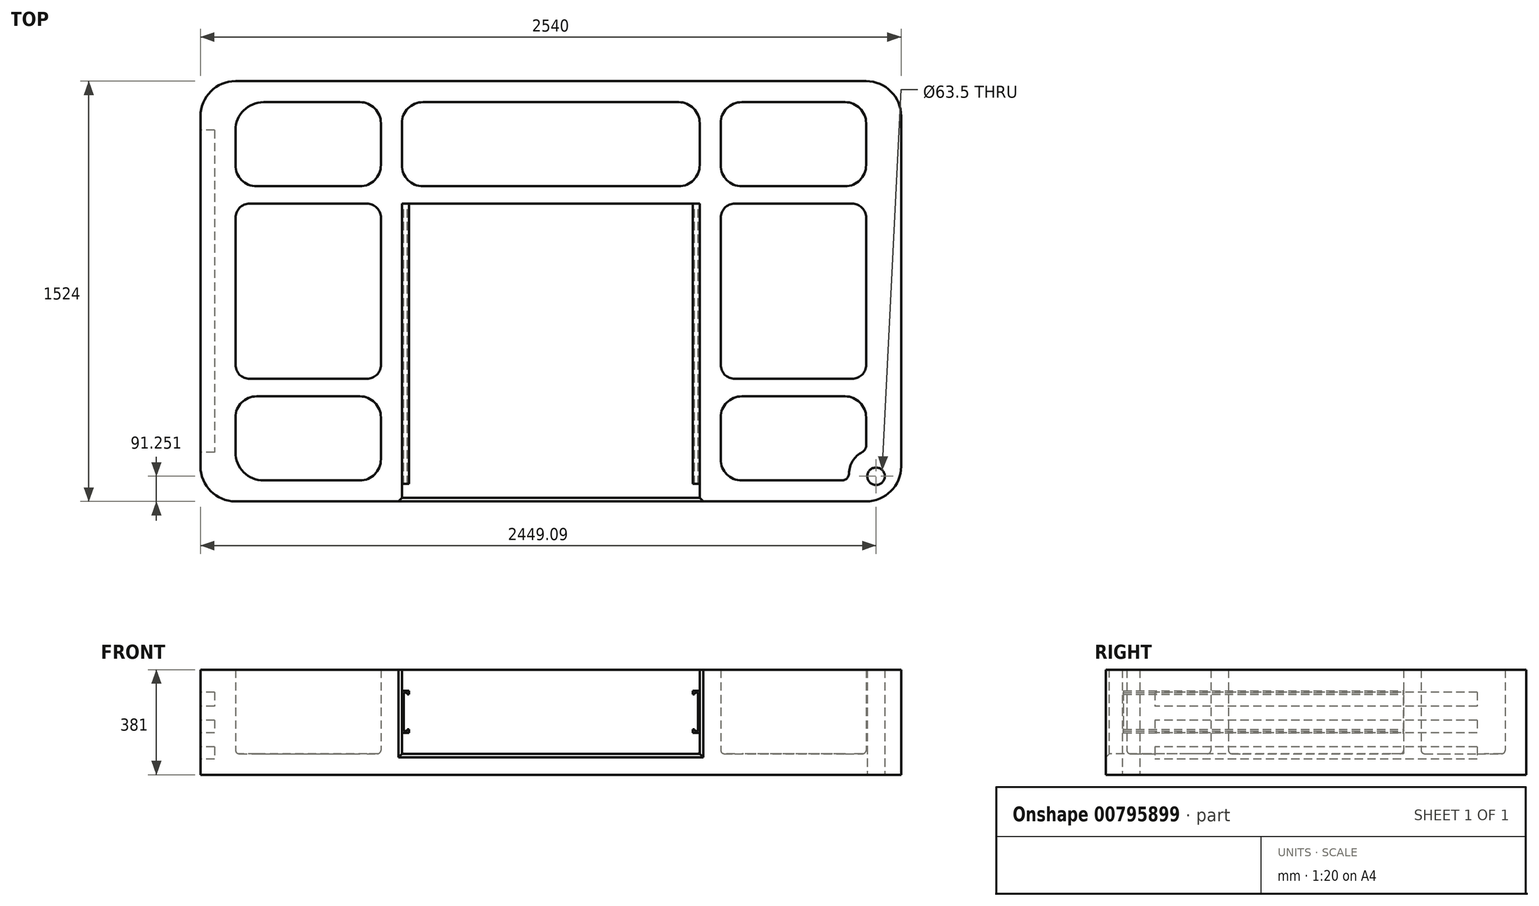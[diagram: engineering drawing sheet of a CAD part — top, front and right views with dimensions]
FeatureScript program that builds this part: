
annotation { "Feature Type Name" : "Feature", "Feature Type Description" : "" }
export const myFeature = defineFeature(function(context is Context, id is Id, definition is map)
    precondition{}
    {
        {
            var Q0;
            Q0=qCreatedBy(makeId("Top.planeOp"),FACE);
            var sketch = newSketch(context, id + "F0", { "sketchPlane" : qUnion([Q0])});
            skLineSegment(sketch, "E0.bottom", {"start": v(-254, 266.7) * mm, "end": v(500.38, 266.7) * mm});
            skLineSegment(sketch, "E0.top", {"start": v(-254, -266.7) * mm, "end": v(500.38, -266.7) * mm});
            skLineSegment(sketch, "E0.left", {"start": v(-254, 266.7) * mm, "end": v(-254, -266.7) * mm});
            skLineSegment(sketch, "E0.right", {"start": v(500.38, 266.7) * mm, "end": v(500.38, -266.7) * mm});
            skSolve(sketch);
        }
        {
            var Q0;
            Q0=qCreatedBy(makeId("Top.planeOp"),FACE);
            var sketch = newSketch(context, id + "F1", { "sketchPlane" : qUnion([Q0])});
            skLineSegment(sketch, "E1.bottom", {"start": v(1270, -762) * mm, "end": v(-1270, -762) * mm});
            skLineSegment(sketch, "E1.top", {"start": v(1270, 762) * mm, "end": v(-1270, 762) * mm});
            skLineSegment(sketch, "E1.left", {"start": v(1270, -762) * mm, "end": v(1270, 762) * mm});
            skLineSegment(sketch, "E1.right", {"start": v(-1270, -762) * mm, "end": v(-1270, 762) * mm});
            skPoint(sketch, "E1.middle", {"position": v(0, 0) * mm});
            skLineSegment(sketch, "E2.bottom", {"start": v(-692.15, 685.8) * mm, "end": v(-1041.4, 685.8) * mm});
            skLineSegment(sketch, "E2.top", {"start": v(-692.15, 381) * mm, "end": v(-1066.8, 381) * mm});
            skLineSegment(sketch, "E2.left", {"start": v(-615.95, 609.6) * mm, "end": v(-615.95, 457.2) * mm});
            skLineSegment(sketch, "E2.right", {"start": v(-1143, 584.2) * mm, "end": v(-1143, 457.2) * mm});
            skPoint(sketch, "E2.middle", {"position": v(-879.48, 533.4) * mm});
            skLineSegment(sketch, "E3.left", {"start": v(-539.75, 609.6) * mm, "end": v(-539.75, 457.2) * mm});
            skPoint(sketch, "E3.middle", {"position": v(0, 528.9) * mm});
            skLineSegment(sketch, "E4", {"start": v(0, 837.18) * mm, "end": v(0, -847.88) * mm, "construction": true});
            skPoint(sketch, "E4.startSnap0", {"position": v(0, 762) * mm});
            skLineSegment(sketch, "E5", {"start": v(-857.73, 0) * mm, "end": v(882.55, 0) * mm, "construction": true});
            skPoint(sketch, "E5.startSnap0", {"position": v(-1270, 0) * mm});
            skLineSegment(sketch, "E6", {"start": v(-463.55, 685.8) * mm, "end": v(0, 685.8) * mm});
            skLineSegment(sketch, "E7", {"start": v(0, 685.8) * mm, "end": v(0, 381) * mm});
            skLineSegment(sketch, "E8", {"start": v(0, 381) * mm, "end": v(-463.55, 381) * mm});
            skLineSegment(sketch, "E9.bottom", {"start": v(-539.75, 317.5) * mm, "end": v(539.75, 317.5) * mm});
            skLineSegment(sketch, "E9.top", {"start": v(-539.75, -317.5) * mm, "end": v(539.75, -317.5) * mm});
            skLineSegment(sketch, "E9.left", {"start": v(-539.75, 317.5) * mm, "end": v(-539.75, -317.5) * mm});
            skLineSegment(sketch, "E9.right", {"start": v(539.75, 317.5) * mm, "end": v(539.75, -317.5) * mm});
            skLineSegment(sketch, "E10.bottom", {"start": v(-1092.2, 317.5) * mm, "end": v(-666.75, 317.5) * mm});
            skLineSegment(sketch, "E10.top", {"start": v(-1092.2, -317.5) * mm, "end": v(-666.75, -317.5) * mm});
            skLineSegment(sketch, "E10.left", {"start": v(-1143, 266.7) * mm, "end": v(-1143, -266.7) * mm});
            skLineSegment(sketch, "E10.right", {"start": v(-615.95, 266.7) * mm, "end": v(-615.95, -266.7) * mm});
            skPoint(sketch, "E10.middle", {"position": v(-879.48, 0) * mm});
            skLineSegment(sketch, "E11.MirrorCS", {"start": v(0, 381) * mm, "end": v(463.55, 381) * mm});
            skLineSegment(sketch, "E12.MirrorCS", {"start": v(539.75, 609.6) * mm, "end": v(539.75, 457.2) * mm});
            skLineSegment(sketch, "E13.MirrorCS", {"start": v(463.55, 685.8) * mm, "end": v(0, 685.8) * mm});
            skLineSegment(sketch, "E14.MirrorCS", {"start": v(692.15, 685.8) * mm, "end": v(1066.8, 685.8) * mm});
            skLineSegment(sketch, "E15.MirrorCS", {"start": v(615.95, 609.6) * mm, "end": v(615.95, 457.2) * mm});
            skLineSegment(sketch, "E16.MirrorCS", {"start": v(692.15, 381) * mm, "end": v(1066.8, 381) * mm});
            skLineSegment(sketch, "E17.MirrorCS", {"start": v(1143, 609.6) * mm, "end": v(1143, 457.2) * mm});
            skLineSegment(sketch, "E18.MirrorCS", {"start": v(615.95, 266.7) * mm, "end": v(615.95, -266.7) * mm});
            skLineSegment(sketch, "E19.MirrorCS", {"start": v(1092.2, -317.5) * mm, "end": v(666.75, -317.5) * mm});
            skLineSegment(sketch, "E20.MirrorCS", {"start": v(1143, 266.7) * mm, "end": v(1143, -266.7) * mm});
            skLineSegment(sketch, "E21.MirrorCS", {"start": v(1092.2, 317.5) * mm, "end": v(666.75, 317.5) * mm});
            skLineSegment(sketch, "E22.MirrorCS", {"start": v(-1143, -584.2) * mm, "end": v(-1143, -457.2) * mm});
            skLineSegment(sketch, "E23.MirrorCS", {"start": v(-692.15, -685.8) * mm, "end": v(-1041.4, -685.8) * mm});
            skLineSegment(sketch, "E24.MirrorCS", {"start": v(-615.95, -609.6) * mm, "end": v(-615.95, -457.2) * mm});
            skLineSegment(sketch, "E25.MirrorCS", {"start": v(-692.15, -381) * mm, "end": v(-1066.8, -381) * mm});
            skLineSegment(sketch, "E26.MirrorCS", {"start": v(0, -381) * mm, "end": v(-463.55, -381) * mm});
            skLineSegment(sketch, "E27.MirrorCS", {"start": v(-539.75, -609.6) * mm, "end": v(-539.75, -457.2) * mm});
            skLineSegment(sketch, "E28.MirrorCS", {"start": v(-463.55, -685.8) * mm, "end": v(0, -685.8) * mm});
            skLineSegment(sketch, "E29.MirrorCS", {"start": v(463.55, -685.8) * mm, "end": v(0, -685.8) * mm});
            skLineSegment(sketch, "E30.MirrorCS", {"start": v(0, -381) * mm, "end": v(463.55, -381) * mm});
            skLineSegment(sketch, "E31.MirrorCS", {"start": v(539.75, -609.6) * mm, "end": v(539.75, -457.2) * mm});
            skLineSegment(sketch, "E32.MirrorCS", {"start": v(692.15, -381) * mm, "end": v(1066.8, -381) * mm});
            skLineSegment(sketch, "E33.MirrorCS", {"start": v(615.95, -609.6) * mm, "end": v(615.95, -457.2) * mm});
            skLineSegment(sketch, "E34.MirrorCS", {"start": v(692.15, -685.8) * mm, "end": v(1066.8, -685.8) * mm});
            skLineSegment(sketch, "E35.MirrorCS", {"start": v(1143, -609.6) * mm, "end": v(1143, -457.2) * mm});
            skPoint(sketch, "E36.visualSharp", {"position": v(615.95, 685.8) * mm});
            skArc(sketch, "E36.filletArc", {"start": v(692.15, 685.8) * mm, "mid": v(638.27, 663.48) * mm, "end": v(615.95, 609.6) * mm});
            skPoint(sketch, "E37.visualSharp", {"position": v(615.95, 381) * mm});
            skArc(sketch, "E37.filletArc", {"start": v(615.95, 457.2) * mm, "mid": v(638.27, 403.32) * mm, "end": v(692.15, 381) * mm});
            skPoint(sketch, "E38.visualSharp", {"position": v(1143, 381) * mm});
            skArc(sketch, "E38.filletArc", {"start": v(1066.8, 381) * mm, "mid": v(1120.68, 403.32) * mm, "end": v(1143, 457.2) * mm});
            skPoint(sketch, "E39.visualSharp", {"position": v(1143, -381) * mm});
            skArc(sketch, "E39.filletArc", {"start": v(1143, -457.2) * mm, "mid": v(1120.68, -403.32) * mm, "end": v(1066.8, -381) * mm});
            skPoint(sketch, "E40.visualSharp", {"position": v(1143, -685.8) * mm});
            skPoint(sketch, "E41.visualSharp", {"position": v(615.95, -381) * mm});
            skArc(sketch, "E41.filletArc", {"start": v(692.15, -381) * mm, "mid": v(638.27, -403.32) * mm, "end": v(615.95, -457.2) * mm});
            skPoint(sketch, "E42.visualSharp", {"position": v(615.95, -685.8) * mm});
            skArc(sketch, "E42.filletArc", {"start": v(615.95, -609.6) * mm, "mid": v(638.27, -663.48) * mm, "end": v(692.15, -685.8) * mm});
            skPoint(sketch, "E43.visualSharp", {"position": v(-615.95, -381) * mm});
            skArc(sketch, "E43.filletArc", {"start": v(-615.95, -457.2) * mm, "mid": v(-638.27, -403.32) * mm, "end": v(-692.15, -381) * mm});
            skPoint(sketch, "E44.visualSharp", {"position": v(-615.95, -685.8) * mm});
            skArc(sketch, "E44.filletArc", {"start": v(-692.15, -685.8) * mm, "mid": v(-638.27, -663.48) * mm, "end": v(-615.95, -609.6) * mm});
            skPoint(sketch, "E45.visualSharp", {"position": v(-1143, -381) * mm});
            skArc(sketch, "E45.filletArc", {"start": v(-1066.8, -381) * mm, "mid": v(-1120.68, -403.32) * mm, "end": v(-1143, -457.2) * mm});
            skPoint(sketch, "E46.visualSharp", {"position": v(-539.75, -381) * mm});
            skArc(sketch, "E46.filletArc", {"start": v(-463.55, -381) * mm, "mid": v(-517.43, -403.32) * mm, "end": v(-539.75, -457.2) * mm});
            skPoint(sketch, "E47.visualSharp", {"position": v(-539.75, -685.8) * mm});
            skArc(sketch, "E47.filletArc", {"start": v(-539.75, -609.6) * mm, "mid": v(-517.43, -663.48) * mm, "end": v(-463.55, -685.8) * mm});
            skPoint(sketch, "E48.visualSharp", {"position": v(539.75, -381) * mm});
            skArc(sketch, "E48.filletArc", {"start": v(539.75, -457.2) * mm, "mid": v(517.43, -403.32) * mm, "end": v(463.55, -381) * mm});
            skPoint(sketch, "E49.visualSharp", {"position": v(539.75, -685.8) * mm});
            skArc(sketch, "E49.filletArc", {"start": v(463.55, -685.8) * mm, "mid": v(517.43, -663.48) * mm, "end": v(539.75, -609.6) * mm});
            skPoint(sketch, "E50.visualSharp", {"position": v(-539.75, 685.8) * mm});
            skArc(sketch, "E50.filletArc", {"start": v(-463.55, 685.8) * mm, "mid": v(-517.43, 663.48) * mm, "end": v(-539.75, 609.6) * mm});
            skPoint(sketch, "E51.visualSharp", {"position": v(-539.75, 381) * mm});
            skArc(sketch, "E51.filletArc", {"start": v(-539.75, 457.2) * mm, "mid": v(-517.43, 403.32) * mm, "end": v(-463.55, 381) * mm});
            skPoint(sketch, "E52.visualSharp", {"position": v(539.75, 685.8) * mm});
            skArc(sketch, "E52.filletArc", {"start": v(539.75, 609.6) * mm, "mid": v(517.43, 663.48) * mm, "end": v(463.55, 685.8) * mm});
            skPoint(sketch, "E53.visualSharp", {"position": v(539.75, 381) * mm});
            skArc(sketch, "E53.filletArc", {"start": v(463.55, 381) * mm, "mid": v(517.43, 403.32) * mm, "end": v(539.75, 457.2) * mm});
            skPoint(sketch, "E54.visualSharp", {"position": v(-615.95, 685.8) * mm});
            skArc(sketch, "E54.filletArc", {"start": v(-615.95, 609.6) * mm, "mid": v(-638.27, 663.48) * mm, "end": v(-692.15, 685.8) * mm});
            skPoint(sketch, "E55.visualSharp", {"position": v(-1143, 685.8) * mm});
            skPoint(sketch, "E56.visualSharp", {"position": v(-1143, 381) * mm});
            skArc(sketch, "E56.filletArc", {"start": v(-1143, 457.2) * mm, "mid": v(-1120.68, 403.32) * mm, "end": v(-1066.8, 381) * mm});
            skPoint(sketch, "E57.visualSharp", {"position": v(-615.95, 381) * mm});
            skArc(sketch, "E57.filletArc", {"start": v(-692.15, 381) * mm, "mid": v(-638.27, 403.32) * mm, "end": v(-615.95, 457.2) * mm});
            skPoint(sketch, "E58.visualSharp", {"position": v(-615.95, 317.5) * mm});
            skArc(sketch, "E58.filletArc", {"start": v(-615.95, 266.7) * mm, "mid": v(-630.83, 302.62) * mm, "end": v(-666.75, 317.5) * mm});
            skPoint(sketch, "E59.visualSharp", {"position": v(-1143, 317.5) * mm});
            skArc(sketch, "E59.filletArc", {"start": v(-1092.2, 317.5) * mm, "mid": v(-1128.12, 302.62) * mm, "end": v(-1143, 266.7) * mm});
            skPoint(sketch, "E60.visualSharp", {"position": v(-1143, -317.5) * mm});
            skArc(sketch, "E60.filletArc", {"start": v(-1143, -266.7) * mm, "mid": v(-1128.12, -302.62) * mm, "end": v(-1092.2, -317.5) * mm});
            skPoint(sketch, "E61.visualSharp", {"position": v(-615.95, -317.5) * mm});
            skArc(sketch, "E61.filletArc", {"start": v(-666.75, -317.5) * mm, "mid": v(-630.83, -302.62) * mm, "end": v(-615.95, -266.7) * mm});
            skPoint(sketch, "E62.visualSharp", {"position": v(615.95, 317.5) * mm});
            skArc(sketch, "E62.filletArc", {"start": v(666.75, 317.5) * mm, "mid": v(630.83, 302.62) * mm, "end": v(615.95, 266.7) * mm});
            skPoint(sketch, "E63.visualSharp", {"position": v(1143, 317.5) * mm});
            skArc(sketch, "E63.filletArc", {"start": v(1143, 266.7) * mm, "mid": v(1128.12, 302.62) * mm, "end": v(1092.2, 317.5) * mm});
            skPoint(sketch, "E64.visualSharp", {"position": v(1143, -317.5) * mm});
            skArc(sketch, "E64.filletArc", {"start": v(1092.2, -317.5) * mm, "mid": v(1128.12, -302.62) * mm, "end": v(1143, -266.7) * mm});
            skPoint(sketch, "E65.visualSharp", {"position": v(615.95, -317.5) * mm});
            skArc(sketch, "E65.filletArc", {"start": v(615.95, -266.7) * mm, "mid": v(630.83, -302.62) * mm, "end": v(666.75, -317.5) * mm});
            skLineSegment(sketch, "E66.MirrorCS", {"start": v(857.73, 0) * mm, "end": v(-882.55, 0) * mm, "construction": true});
            skArc(sketch, "E67.filletArc", {"start": v(-1143, -584.2) * mm, "mid": v(-1113.24, -656.04) * mm, "end": v(-1041.4, -685.8) * mm});
            skArc(sketch, "E68.filletArc", {"start": v(-1041.4, 685.8) * mm, "mid": v(-1113.24, 656.04) * mm, "end": v(-1143, 584.2) * mm});
            skArc(sketch, "E69.filletArc", {"start": v(1143, 609.6) * mm, "mid": v(1120.68, 663.48) * mm, "end": v(1066.8, 685.8) * mm});
            skArc(sketch, "E70.filletArc", {"start": v(1066.8, -685.8) * mm, "mid": v(1120.68, -663.48) * mm, "end": v(1143, -609.6) * mm});
            skSolve(sketch);
        }
        {
            var Q0;
            Q0=qSketchRegion(id+"F1",true);
            extrude(context, id + "F2", {"entities" : qUnion([Q0]), "depth" : 381 * mm, "offsetDistance" : 25.4 * mm});
        }
        {
            var Q0;
            Q0=makeQuery(id+"F2.opExtrude","SWEPT_EDGE",EDGE,{"disambiguationData":[OSD([sQuery(id+"F1.wireOp",EDGE,"E1.bottom"),sQuery(id+"F1.wireOp",EDGE,"E1.right")])]});
            var Q1;
            Q1=makeQuery(id+"F2.opExtrude","SWEPT_EDGE",EDGE,{"disambiguationData":[OSD([sQuery(id+"F1.wireOp",EDGE,"E1.bottom"),sQuery(id+"F1.wireOp",EDGE,"E1.left")])]});
            var Q2;
            Q2=makeQuery(id+"F2.opExtrude","SWEPT_EDGE",EDGE,{"disambiguationData":[OSD([sQuery(id+"F1.wireOp",EDGE,"E1.top"),sQuery(id+"F1.wireOp",EDGE,"E1.right")])]});
            var Q3;
            Q3=makeQuery(id+"F2.opExtrude","SWEPT_EDGE",EDGE,{"disambiguationData":[OSD([sQuery(id+"F1.wireOp",EDGE,"E1.top"),sQuery(id+"F1.wireOp",EDGE,"E1.left")])]});
            fillet(context, id + "F3", {"entities" : qUnion([Q0, Q1, Q2, Q3]), "radius" : 127 * mm, "tangentPropagation" : true, "allowEdgeOverflow" : false});
        }
        {
            var Q0;
            Q0=makeQuery(id+"F2.opExtrude","CAP_FACE",FACE,{"disambiguationData":[OSD([sQuery(id+"F1.wireOp",EDGE,"E1.bottom"),sQuery(id+"F1.wireOp",EDGE,"E1.top"),sQuery(id+"F1.wireOp",EDGE,"E1.left"),sQuery(id+"F1.wireOp",EDGE,"E1.right")])],"isStart":false});
            var sketch = newSketch(context, id + "F4", { "sketchPlane" : qUnion([Q0])});
            skSolve(sketch);
        }
        {
            var Q0;
            Q0=makeQuery(id+"F2.opExtrude","CAP_FACE",FACE,{"disambiguationData":[OSD([sQuery(id+"F1.wireOp",EDGE,"E1.bottom"),sQuery(id+"F1.wireOp",EDGE,"E1.top"),sQuery(id+"F1.wireOp",EDGE,"E1.left"),sQuery(id+"F1.wireOp",EDGE,"E1.right"),sQuery(id+"F1.wireOp",EDGE,"E2.bottom"),sQuery(id+"F1.wireOp",EDGE,"E2.top"),sQuery(id+"F1.wireOp",EDGE,"E2.left"),sQuery(id+"F1.wireOp",EDGE,"E2.right"),sQuery(id+"F1.wireOp",EDGE,"E3.left"),sQuery(id+"F1.wireOp",EDGE,"E6"),sQuery(id+"F1.wireOp",EDGE,"E8"),sQuery(id+"F1.wireOp",EDGE,"E9.bottom"),sQuery(id+"F1.wireOp",EDGE,"E9.top"),sQuery(id+"F1.wireOp",EDGE,"E9.left"),sQuery(id+"F1.wireOp",EDGE,"E9.right"),sQuery(id+"F1.wireOp",EDGE,"E10.bottom"),sQuery(id+"F1.wireOp",EDGE,"E10.top"),sQuery(id+"F1.wireOp",EDGE,"E10.left"),sQuery(id+"F1.wireOp",EDGE,"E10.right"),sQuery(id+"F1.wireOp",EDGE,"E11.MirrorCS"),sQuery(id+"F1.wireOp",EDGE,"E12.MirrorCS"),sQuery(id+"F1.wireOp",EDGE,"E13.MirrorCS"),sQuery(id+"F1.wireOp",EDGE,"E14.MirrorCS"),sQuery(id+"F1.wireOp",EDGE,"E15.MirrorCS"),sQuery(id+"F1.wireOp",EDGE,"E16.MirrorCS"),sQuery(id+"F1.wireOp",EDGE,"E17.MirrorCS"),sQuery(id+"F1.wireOp",EDGE,"E18.MirrorCS"),sQuery(id+"F1.wireOp",EDGE,"E19.MirrorCS"),sQuery(id+"F1.wireOp",EDGE,"E20.MirrorCS"),sQuery(id+"F1.wireOp",EDGE,"E21.MirrorCS"),sQuery(id+"F1.wireOp",EDGE,"E22.MirrorCS"),sQuery(id+"F1.wireOp",EDGE,"E23.MirrorCS"),sQuery(id+"F1.wireOp",EDGE,"E24.MirrorCS"),sQuery(id+"F1.wireOp",EDGE,"E25.MirrorCS"),sQuery(id+"F1.wireOp",EDGE,"E26.MirrorCS"),sQuery(id+"F1.wireOp",EDGE,"E27.MirrorCS"),sQuery(id+"F1.wireOp",EDGE,"E28.MirrorCS"),sQuery(id+"F1.wireOp",EDGE,"E29.MirrorCS"),sQuery(id+"F1.wireOp",EDGE,"E30.MirrorCS"),sQuery(id+"F1.wireOp",EDGE,"E31.MirrorCS"),sQuery(id+"F1.wireOp",EDGE,"E32.MirrorCS"),sQuery(id+"F1.wireOp",EDGE,"E33.MirrorCS"),sQuery(id+"F1.wireOp",EDGE,"E34.MirrorCS"),sQuery(id+"F1.wireOp",EDGE,"E35.MirrorCS"),sQuery(id+"F1.wireOp",EDGE,"6bad22d6-b295-4cfd-84df-ab09200a6259.filletArc"),sQuery(id+"F1.wireOp",EDGE,"E36.filletArc"),sQuery(id+"F1.wireOp",EDGE,"E37.filletArc"),sQuery(id+"F1.wireOp",EDGE,"E38.filletArc"),sQuery(id+"F1.wireOp",EDGE,"E39.filletArc"),sQuery(id+"F1.wireOp",EDGE,"E40.filletArc"),sQuery(id+"F1.wireOp",EDGE,"E41.filletArc"),sQuery(id+"F1.wireOp",EDGE,"E42.filletArc"),sQuery(id+"F1.wireOp",EDGE,"E43.filletArc"),sQuery(id+"F1.wireOp",EDGE,"E44.filletArc"),sQuery(id+"F1.wireOp",EDGE,"8417e481-1a63-4eb4-b0fb-f845a37859cb.filletArc"),sQuery(id+"F1.wireOp",EDGE,"E45.filletArc"),sQuery(id+"F1.wireOp",EDGE,"E46.filletArc"),sQuery(id+"F1.wireOp",EDGE,"E47.filletArc"),sQuery(id+"F1.wireOp",EDGE,"E48.filletArc"),sQuery(id+"F1.wireOp",EDGE,"E49.filletArc"),sQuery(id+"F1.wireOp",EDGE,"E50.filletArc"),sQuery(id+"F1.wireOp",EDGE,"E51.filletArc"),sQuery(id+"F1.wireOp",EDGE,"E52.filletArc"),sQuery(id+"F1.wireOp",EDGE,"E53.filletArc"),sQuery(id+"F1.wireOp",EDGE,"E54.filletArc"),sQuery(id+"F1.wireOp",EDGE,"E55.filletArc"),sQuery(id+"F1.wireOp",EDGE,"E56.filletArc"),sQuery(id+"F1.wireOp",EDGE,"E57.filletArc"),sQuery(id+"F1.wireOp",EDGE,"E58.filletArc"),sQuery(id+"F1.wireOp",EDGE,"E59.filletArc"),sQuery(id+"F1.wireOp",EDGE,"E60.filletArc"),sQuery(id+"F1.wireOp",EDGE,"E61.filletArc"),sQuery(id+"F1.wireOp",EDGE,"E62.filletArc"),sQuery(id+"F1.wireOp",EDGE,"E63.filletArc"),sQuery(id+"F1.wireOp",EDGE,"E64.filletArc"),sQuery(id+"F1.wireOp",EDGE,"E65.filletArc")])],"isStart":true});
            var sketch = newSketch(context, id + "F5", { "sketchPlane" : qUnion([Q0])});
            skArc(sketch, "E71.0", {"start": v(-1143, 762) * mm, "mid": v(-1232.8, 724.8) * mm, "end": v(-1270, 635) * mm});
            skLineSegment(sketch, "E71.1", {"start": v(1143, 762) * mm, "end": v(-1143, 762) * mm});
            skArc(sketch, "E71.2", {"start": v(1270, 635) * mm, "mid": v(1232.8, 724.8) * mm, "end": v(1143, 762) * mm});
            skLineSegment(sketch, "E71.3", {"start": v(1270, 635) * mm, "end": v(1270, -635) * mm});
            skArc(sketch, "E71.4", {"start": v(1143, -762) * mm, "mid": v(1232.8, -724.8) * mm, "end": v(1270, -635) * mm});
            skLineSegment(sketch, "E71.5", {"start": v(1143, -762) * mm, "end": v(-1143, -762) * mm});
            skArc(sketch, "E71.6", {"start": v(-1270, -635) * mm, "mid": v(-1232.8, -724.8) * mm, "end": v(-1143, -762) * mm});
            skLineSegment(sketch, "E71.7", {"start": v(-1270, 635) * mm, "end": v(-1270, -635) * mm});
            skSolve(sketch);
        }
        {
            var Q0;
            Q0 = qSketchRegion(id + "F5", true);
            extrude(context, id + "F6", {"entities" : qUnion([Q0]), "operationType" : NewBodyOperationType.ADD, "oppositeDirection" : true, "depth" : 76.2 * mm, "offsetDistance" : 25.4 * mm});
        }
        {
            var Q0;
            {var subQ34=sQuery(id+"F1.wireOp",EDGE,"E2.bottom");Q0=makeQuery(id+"F4.imprint","IMPRINT",FACE,{"disambiguationData":[TD([[makeQuery(id+"F4.imprint","IMPRINT",EDGE,{"derivedFrom":makeQuery(id+"F2.opExtrude","CAP_EDGE",EDGE,{"disambiguationData":[OSD([subQ34])],"isStart":false})}),-1.0]])]});}
            var sketch = newSketch(context, id + "F7", { "sketchPlane" : qUnion([Q0])});
            skLineSegment(sketch, "E72.bottom", {"start": v(-539.75, -288.84) * mm, "end": v(539.75, -288.84) * mm});
            skLineSegment(sketch, "E72.top", {"start": v(-539.75, -796.84) * mm, "end": v(539.75, -796.84) * mm});
            skLineSegment(sketch, "E72.left", {"start": v(-539.75, -288.84) * mm, "end": v(-539.75, -796.84) * mm});
            skLineSegment(sketch, "E72.right", {"start": v(539.75, -288.84) * mm, "end": v(539.75, -796.84) * mm});
            skSolve(sketch);
        }
        {
            var Q0;
            Q0 = qSketchRegion(id + "F7", true);
            var Q1;
            Q1=makeQuery(id+"F6.boolean.opBoolean","SPLIT",FACE,{"disambiguationData":[TD([makeQuery(id+"F2.opExtrude","SWEPT_FACE",FACE,{"disambiguationData":[OSD([sQuery(id+"F1.wireOp",EDGE,"E9.bottom")])]})])],"derivedFrom":makeQuery(id+"F6.opExtrude","CAP_FACE",FACE,{"disambiguationData":[OSD([sQuery(id+"F5.wireOp",EDGE,"E71.0"),sQuery(id+"F5.wireOp",EDGE,"E71.1"),sQuery(id+"F5.wireOp",EDGE,"E71.2"),sQuery(id+"F5.wireOp",EDGE,"E71.3"),sQuery(id+"F5.wireOp",EDGE,"E71.4"),sQuery(id+"F5.wireOp",EDGE,"E71.5"),sQuery(id+"F5.wireOp",EDGE,"E71.6"),sQuery(id+"F5.wireOp",EDGE,"E71.7")])],"isStart":false})});
            extrude(context, id + "F8", {"entities" : qUnion([Q0]), "operationType" : NewBodyOperationType.REMOVE, "endBound" : BoundingType.UP_TO_SURFACE, "oppositeDirection" : true, "depth" : 25.4 * mm, "endBoundEntityFace" : qUnion([Q1]), "offsetDistance" : 25.4 * mm});
        }
        {
            var Q0;
            Q0=makeQuery(id+"F2.opExtrude","SWEPT_FACE",FACE,{"disambiguationData":[OSD([sQuery(id+"F1.wireOp",EDGE,"E1.right")])]});
            var sketch = newSketch(context, id + "F9", { "sketchPlane" : qUnion([Q0])});
            skLineSegment(sketch, "E73.bottom", {"start": v(-584.2, 299.43) * mm, "end": v(584.2, 299.43) * mm});
            skLineSegment(sketch, "E73.top", {"start": v(-584.2, 248.63) * mm, "end": v(584.2, 248.63) * mm});
            skLineSegment(sketch, "E73.left", {"start": v(-584.2, 299.43) * mm, "end": v(-584.2, 248.63) * mm});
            skLineSegment(sketch, "E73.right", {"start": v(584.2, 299.43) * mm, "end": v(584.2, 248.63) * mm});
            skLineSegment(sketch, "E74.bottom", {"start": v(-584.2, 197.83) * mm, "end": v(584.2, 197.83) * mm});
            skLineSegment(sketch, "E74.top", {"start": v(-584.2, 151.8) * mm, "end": v(584.2, 151.8) * mm});
            skLineSegment(sketch, "E74.left", {"start": v(-584.2, 197.83) * mm, "end": v(-584.2, 151.8) * mm});
            skLineSegment(sketch, "E74.right", {"start": v(584.2, 197.83) * mm, "end": v(584.2, 151.8) * mm});
            skLineSegment(sketch, "E75.bottom", {"start": v(-584.2, 101) * mm, "end": v(584.2, 101) * mm});
            skLineSegment(sketch, "E75.top", {"start": v(-584.2, 57.1) * mm, "end": v(584.2, 57.1) * mm});
            skLineSegment(sketch, "E75.left", {"start": v(-584.2, 101) * mm, "end": v(-584.2, 57.1) * mm});
            skLineSegment(sketch, "E75.right", {"start": v(584.2, 101) * mm, "end": v(584.2, 57.1) * mm});
            skSolve(sketch);
        }
        {
            var Q0;
            Q0 = qSketchRegion(id + "F9", true);
            extrude(context, id + "F10", {"entities" : qUnion([Q0]), "operationType" : NewBodyOperationType.REMOVE, "oppositeDirection" : true, "depth" : 50.8 * mm, "offsetDistance" : 25.4 * mm});
        }
        {
            var Q0;
            Q0=makeQuery(id+"F8.boolean.opBoolean","INTERSECT",EDGE,{"derivedFrom":[makeQuery(id+"F2.opExtrude","SWEPT_FACE",FACE,{"disambiguationData":[OSD([sQuery(id+"F1.wireOp",EDGE,"E1.bottom")])]}),makeQuery(id+"F8.opExtrude","SWEPT_FACE",FACE,{"disambiguationData":[OSD([sQuery(id+"F7.wireOp",EDGE,"E72.left")])]})]});
            var Q1;
            Q1=makeQuery(id+"F8.boolean.opBoolean","INTERSECT",EDGE,{"derivedFrom":[makeQuery(id+"F2.opExtrude","SWEPT_FACE",FACE,{"disambiguationData":[OSD([sQuery(id+"F1.wireOp",EDGE,"E1.bottom")])]}),makeQuery(id+"F8.opExtrude","SWEPT_FACE",FACE,{"disambiguationData":[OSD([sQuery(id+"F7.wireOp",EDGE,"E72.right")])]})]});
            var Q2;
            Q2=makeQuery(id+"F8.boolean.opBoolean","INTERSECT",EDGE,{"derivedFrom":[makeQuery(id+"F2.opExtrude","SWEPT_FACE",FACE,{"disambiguationData":[OSD([sQuery(id+"F1.wireOp",EDGE,"E1.bottom")])]}),makeQuery(id+"F8.opExtrude","CAP_FACE",FACE,{"disambiguationData":[OSD([sQuery(id+"F7.wireOp",EDGE,"E72.bottom"),sQuery(id+"F7.wireOp",EDGE,"E72.top"),sQuery(id+"F7.wireOp",EDGE,"E72.left"),sQuery(id+"F7.wireOp",EDGE,"E72.right")])],"isStart":false})]});
            chamfer(context, id + "F11", {"entities" : qUnion([Q0, Q1, Q2]), "width" : 12.7 * mm, "tangentPropagation" : true});
        }
        {
            var Q0;
            Q0=makeQuery(id+"F2.opExtrude","SWEPT_FACE",FACE,{"disambiguationData":[OSD([sQuery(id+"F1.wireOp",EDGE,"E9.bottom")])]});
            var sketch = newSketch(context, id + "F12", { "sketchPlane" : qUnion([Q0])});
            skLineSegment(sketch, "E76", {"start": v(621.6, 228.6) * mm, "end": v(-605.2, 228.6) * mm, "construction": true});
            skPoint(sketch, "E76.startSnap0", {"position": v(539.75, 228.6) * mm});
            skLineSegment(sketch, "E77", {"start": v(539.75, 228.6) * mm, "end": v(539.75, 304.8) * mm});
            skLineSegment(sketch, "E78", {"start": v(539.75, 304.8) * mm, "end": v(514.35, 304.8) * mm});
            skLineSegment(sketch, "E79", {"start": v(514.35, 304.8) * mm, "end": v(514.35, 292.1) * mm});
            skLineSegment(sketch, "E80", {"start": v(514.35, 292.1) * mm, "end": v(520.7, 292.1) * mm});
            skLineSegment(sketch, "E81", {"start": v(520.7, 292.1) * mm, "end": v(520.7, 298.45) * mm});
            skLineSegment(sketch, "E82", {"start": v(520.7, 298.45) * mm, "end": v(533.4, 298.45) * mm});
            skLineSegment(sketch, "E83", {"start": v(533.4, 298.45) * mm, "end": v(533.4, 228.6) * mm});
            skLineSegment(sketch, "E84.MirrorCS", {"start": v(514.35, 165.1) * mm, "end": v(520.7, 165.1) * mm});
            skLineSegment(sketch, "E85.MirrorCS", {"start": v(520.7, 165.1) * mm, "end": v(520.7, 158.75) * mm});
            skLineSegment(sketch, "E86.MirrorCS", {"start": v(533.4, 158.75) * mm, "end": v(533.4, 228.6) * mm});
            skLineSegment(sketch, "E87.MirrorCS", {"start": v(520.7, 158.75) * mm, "end": v(533.4, 158.75) * mm});
            skLineSegment(sketch, "E88.MirrorCS", {"start": v(514.35, 152.4) * mm, "end": v(514.35, 165.1) * mm});
            skLineSegment(sketch, "E89.MirrorCS", {"start": v(539.75, 228.6) * mm, "end": v(539.75, 152.4) * mm});
            skLineSegment(sketch, "E90.MirrorCS", {"start": v(539.75, 152.4) * mm, "end": v(514.35, 152.4) * mm});
            skLineSegment(sketch, "E91", {"start": v(0, 348.91) * mm, "end": v(0, 129.74) * mm, "construction": true});
            skLineSegment(sketch, "E92.MirrorCS", {"start": v(-520.7, 165.1) * mm, "end": v(-520.7, 158.75) * mm});
            skLineSegment(sketch, "E93.MirrorCS", {"start": v(-514.35, 165.1) * mm, "end": v(-520.7, 165.1) * mm});
            skLineSegment(sketch, "E94.MirrorCS", {"start": v(-514.35, 152.4) * mm, "end": v(-514.35, 165.1) * mm});
            skLineSegment(sketch, "E95.MirrorCS", {"start": v(-520.7, 158.75) * mm, "end": v(-533.4, 158.75) * mm});
            skLineSegment(sketch, "E96.MirrorCS", {"start": v(-533.4, 158.75) * mm, "end": v(-533.4, 228.6) * mm});
            skLineSegment(sketch, "E97.MirrorCS", {"start": v(-539.75, 228.6) * mm, "end": v(-539.75, 152.4) * mm});
            skLineSegment(sketch, "E98.MirrorCS", {"start": v(-539.75, 152.4) * mm, "end": v(-514.35, 152.4) * mm});
            skLineSegment(sketch, "E99.MirrorCS", {"start": v(-520.7, 292.1) * mm, "end": v(-520.7, 298.45) * mm});
            skLineSegment(sketch, "E100.MirrorCS", {"start": v(-514.35, 292.1) * mm, "end": v(-520.7, 292.1) * mm});
            skLineSegment(sketch, "E101.MirrorCS", {"start": v(-539.75, 304.8) * mm, "end": v(-514.35, 304.8) * mm});
            skLineSegment(sketch, "E102.MirrorCS", {"start": v(-514.35, 304.8) * mm, "end": v(-514.35, 292.1) * mm});
            skLineSegment(sketch, "E103.MirrorCS", {"start": v(-520.7, 298.45) * mm, "end": v(-533.4, 298.45) * mm});
            skLineSegment(sketch, "E104.MirrorCS", {"start": v(-539.75, 228.6) * mm, "end": v(-539.75, 304.8) * mm});
            skLineSegment(sketch, "E105.MirrorCS", {"start": v(-533.4, 298.45) * mm, "end": v(-533.4, 228.6) * mm});
            skSolve(sketch);
        }
        {
            var Q0;
            Q0=makeQuery(id+"F12.imprint","IMPRINT",FACE,{"disambiguationData":[TD([[makeQuery(id+"F12.imprint","IMPRINT",EDGE,{"derivedFrom":sQuery(id+"F12.wireOp",EDGE,"E77")}),-1.0]])]});
            var Q1;
            Q1=makeQuery(id+"F12.imprint","IMPRINT",FACE,{"disambiguationData":[TD([[makeQuery(id+"F12.imprint","IMPRINT",EDGE,{"derivedFrom":sQuery(id+"F12.wireOp",EDGE,"E92.MirrorCS")}),1.0]])]});
            extrude(context, id + "F13", {"entities" : qUnion([Q0, Q1]), "operationType" : NewBodyOperationType.ADD, "depth" : 1016 * mm, "offsetDistance" : 25.4 * mm});
        }
        {
            var Q0;
            Q0=qCreatedBy(makeId("Right.planeOp"),FACE);
            cPlane(context, id + "F14", {"entities" : qUnion([Q0]), "cplaneType" : CPlaneType.OFFSET, "offset" : 812.8 * mm, "width" : 152.4 * mm, "height" : 152.4 * mm});
        }
        {
            var Q0;
            Q0=qCreatedBy(makeId("Top.planeOp"),FACE);
            var sketch = newSketch(context, id + "F15", { "sketchPlane" : qUnion([Q0])});
            skCircle(sketch, "E106", {"center": v(1179.1, -670.75) * mm, "radius": 31.75 * mm});
            skSolve(sketch);
        }
        {
            var Q0;
            Q0=qCreatedBy(makeId("Top.planeOp"),FACE);
            var sketch = newSketch(context, id + "F16", { "sketchPlane" : qUnion([Q0])});
            skCircle(sketch, "E107", {"center": v(1169.93, -661.95) * mm, "radius": 88.9 * mm});
            skSolve(sketch);
        }
        {
            var Q0;
            Q0 = qSketchRegion(id + "F16", true);
            var Q1;
            Q1=makeQuery(id+"F2.opExtrude","SWEPT_BODY",BODY,{"disambiguationData":[OSD([sQuery(id+"F1.wireOp",EDGE,"E1.bottom"),sQuery(id+"F1.wireOp",EDGE,"E1.top"),sQuery(id+"F1.wireOp",EDGE,"E1.left"),sQuery(id+"F1.wireOp",EDGE,"E1.right"),sQuery(id+"F1.wireOp",EDGE,"E2.bottom"),sQuery(id+"F1.wireOp",EDGE,"E2.top"),sQuery(id+"F1.wireOp",EDGE,"E2.left"),sQuery(id+"F1.wireOp",EDGE,"E2.right"),sQuery(id+"F1.wireOp",EDGE,"E3.left"),sQuery(id+"F1.wireOp",EDGE,"E6"),sQuery(id+"F1.wireOp",EDGE,"E8"),sQuery(id+"F1.wireOp",EDGE,"E9.bottom"),sQuery(id+"F1.wireOp",EDGE,"E9.top"),sQuery(id+"F1.wireOp",EDGE,"E9.left"),sQuery(id+"F1.wireOp",EDGE,"E9.right"),sQuery(id+"F1.wireOp",EDGE,"E10.bottom"),sQuery(id+"F1.wireOp",EDGE,"E10.top"),sQuery(id+"F1.wireOp",EDGE,"E10.left"),sQuery(id+"F1.wireOp",EDGE,"E10.right"),sQuery(id+"F1.wireOp",EDGE,"E11.MirrorCS"),sQuery(id+"F1.wireOp",EDGE,"E12.MirrorCS"),sQuery(id+"F1.wireOp",EDGE,"E13.MirrorCS"),sQuery(id+"F1.wireOp",EDGE,"E14.MirrorCS"),sQuery(id+"F1.wireOp",EDGE,"E15.MirrorCS"),sQuery(id+"F1.wireOp",EDGE,"E16.MirrorCS"),sQuery(id+"F1.wireOp",EDGE,"E17.MirrorCS"),sQuery(id+"F1.wireOp",EDGE,"E18.MirrorCS"),sQuery(id+"F1.wireOp",EDGE,"E19.MirrorCS"),sQuery(id+"F1.wireOp",EDGE,"E20.MirrorCS"),sQuery(id+"F1.wireOp",EDGE,"E21.MirrorCS"),sQuery(id+"F1.wireOp",EDGE,"E22.MirrorCS"),sQuery(id+"F1.wireOp",EDGE,"E23.MirrorCS"),sQuery(id+"F1.wireOp",EDGE,"E24.MirrorCS"),sQuery(id+"F1.wireOp",EDGE,"E25.MirrorCS"),sQuery(id+"F1.wireOp",EDGE,"E26.MirrorCS"),sQuery(id+"F1.wireOp",EDGE,"E27.MirrorCS"),sQuery(id+"F1.wireOp",EDGE,"E28.MirrorCS"),sQuery(id+"F1.wireOp",EDGE,"E29.MirrorCS"),sQuery(id+"F1.wireOp",EDGE,"E30.MirrorCS"),sQuery(id+"F1.wireOp",EDGE,"E31.MirrorCS"),sQuery(id+"F1.wireOp",EDGE,"E32.MirrorCS"),sQuery(id+"F1.wireOp",EDGE,"E33.MirrorCS"),sQuery(id+"F1.wireOp",EDGE,"E34.MirrorCS"),sQuery(id+"F1.wireOp",EDGE,"E35.MirrorCS"),sQuery(id+"F1.wireOp",EDGE,"E36.filletArc"),sQuery(id+"F1.wireOp",EDGE,"E37.filletArc"),sQuery(id+"F1.wireOp",EDGE,"E38.filletArc"),sQuery(id+"F1.wireOp",EDGE,"E39.filletArc"),sQuery(id+"F1.wireOp",EDGE,"E41.filletArc"),sQuery(id+"F1.wireOp",EDGE,"E42.filletArc"),sQuery(id+"F1.wireOp",EDGE,"E43.filletArc"),sQuery(id+"F1.wireOp",EDGE,"E44.filletArc"),sQuery(id+"F1.wireOp",EDGE,"E45.filletArc"),sQuery(id+"F1.wireOp",EDGE,"E46.filletArc"),sQuery(id+"F1.wireOp",EDGE,"E47.filletArc"),sQuery(id+"F1.wireOp",EDGE,"E48.filletArc"),sQuery(id+"F1.wireOp",EDGE,"E49.filletArc"),sQuery(id+"F1.wireOp",EDGE,"E50.filletArc"),sQuery(id+"F1.wireOp",EDGE,"E51.filletArc"),sQuery(id+"F1.wireOp",EDGE,"E52.filletArc"),sQuery(id+"F1.wireOp",EDGE,"E53.filletArc"),sQuery(id+"F1.wireOp",EDGE,"E54.filletArc"),sQuery(id+"F1.wireOp",EDGE,"E56.filletArc"),sQuery(id+"F1.wireOp",EDGE,"E57.filletArc"),sQuery(id+"F1.wireOp",EDGE,"E58.filletArc"),sQuery(id+"F1.wireOp",EDGE,"E59.filletArc"),sQuery(id+"F1.wireOp",EDGE,"E60.filletArc"),sQuery(id+"F1.wireOp",EDGE,"E61.filletArc"),sQuery(id+"F1.wireOp",EDGE,"E62.filletArc"),sQuery(id+"F1.wireOp",EDGE,"E63.filletArc"),sQuery(id+"F1.wireOp",EDGE,"E64.filletArc"),sQuery(id+"F1.wireOp",EDGE,"E65.filletArc"),sQuery(id+"F1.wireOp",EDGE,"E67.filletArc"),sQuery(id+"F1.wireOp",EDGE,"E68.filletArc"),sQuery(id+"F1.wireOp",EDGE,"E69.filletArc"),sQuery(id+"F1.wireOp",EDGE,"E70.filletArc")])]});
            extrude(context, id + "F17", {"entities" : qUnion([Q0]), "operationType" : NewBodyOperationType.ADD, "depth" : 381 * mm, "endBoundEntityBody" : qUnion([Q1]), "offsetDistance" : 25.4 * mm});
        }
        {
            var Q0;
            Q0 = qSketchRegion(id + "F15", true);
            extrude(context, id + "F18", {"entities" : qUnion([Q0]), "operationType" : NewBodyOperationType.REMOVE, "endBound" : BoundingType.UP_TO_NEXT, "depth" : 25.4 * mm, "offsetDistance" : 25.4 * mm});
        }
        {
            var Q0;
            Q0=makeQuery(id+"F17.boolean.opBoolean","INTERSECT",EDGE,{"derivedFrom":[makeQuery(id+"F2.opExtrude","SWEPT_FACE",FACE,{"disambiguationData":[OSD([sQuery(id+"F1.wireOp",EDGE,"E35.MirrorCS")])]}),makeQuery(id+"F17.opExtrude","SWEPT_FACE",FACE,{"disambiguationData":[OSD([sQuery(id+"F16.wireOp",EDGE,"E107")])]})]});
            var Q1;
            Q1=makeQuery(id+"F17.boolean.opBoolean","INTERSECT",EDGE,{"derivedFrom":[makeQuery(id+"F2.opExtrude","SWEPT_FACE",FACE,{"disambiguationData":[OSD([sQuery(id+"F1.wireOp",EDGE,"E70.filletArc")])]}),makeQuery(id+"F17.opExtrude","SWEPT_FACE",FACE,{"disambiguationData":[OSD([sQuery(id+"F16.wireOp",EDGE,"E107")])]})]});
            fillet(context, id + "F19", {"entities" : qUnion([Q0, Q1]), "radius" : 25.4 * mm, "tangentPropagation" : true, "allowEdgeOverflow" : false});
        }
        {
            var Q0;
            Q0=makeQuery(id+"F6.boolean.opBoolean","SPLIT",FACE,{"disambiguationData":[TD([makeQuery(id+"F2.opExtrude","SWEPT_FACE",FACE,{"disambiguationData":[OSD([sQuery(id+"F1.wireOp",EDGE,"E3.left")])]})])],"derivedFrom":makeQuery(id+"F6.opExtrude","CAP_FACE",FACE,{"disambiguationData":[OSD([sQuery(id+"F5.wireOp",EDGE,"E71.0"),sQuery(id+"F5.wireOp",EDGE,"E71.1"),sQuery(id+"F5.wireOp",EDGE,"E71.2"),sQuery(id+"F5.wireOp",EDGE,"E71.3"),sQuery(id+"F5.wireOp",EDGE,"E71.4"),sQuery(id+"F5.wireOp",EDGE,"E71.5"),sQuery(id+"F5.wireOp",EDGE,"E71.6"),sQuery(id+"F5.wireOp",EDGE,"E71.7")])],"isStart":false})});
            var Q1;
            Q1=makeQuery(id+"F6.boolean.opBoolean","SPLIT",FACE,{"disambiguationData":[TD([makeQuery(id+"F2.opExtrude","SWEPT_FACE",FACE,{"disambiguationData":[OSD([sQuery(id+"F1.wireOp",EDGE,"E14.MirrorCS")])]})])],"derivedFrom":makeQuery(id+"F6.opExtrude","CAP_FACE",FACE,{"disambiguationData":[OSD([sQuery(id+"F5.wireOp",EDGE,"E71.0"),sQuery(id+"F5.wireOp",EDGE,"E71.1"),sQuery(id+"F5.wireOp",EDGE,"E71.2"),sQuery(id+"F5.wireOp",EDGE,"E71.3"),sQuery(id+"F5.wireOp",EDGE,"E71.4"),sQuery(id+"F5.wireOp",EDGE,"E71.5"),sQuery(id+"F5.wireOp",EDGE,"E71.6"),sQuery(id+"F5.wireOp",EDGE,"E71.7")])],"isStart":false})});
            var Q2;
            Q2=makeQuery(id+"F6.boolean.opBoolean","SPLIT",FACE,{"disambiguationData":[TD([makeQuery(id+"F2.opExtrude","SWEPT_FACE",FACE,{"disambiguationData":[OSD([sQuery(id+"F1.wireOp",EDGE,"E18.MirrorCS")])]})])],"derivedFrom":makeQuery(id+"F6.opExtrude","CAP_FACE",FACE,{"disambiguationData":[OSD([sQuery(id+"F5.wireOp",EDGE,"E71.0"),sQuery(id+"F5.wireOp",EDGE,"E71.1"),sQuery(id+"F5.wireOp",EDGE,"E71.2"),sQuery(id+"F5.wireOp",EDGE,"E71.3"),sQuery(id+"F5.wireOp",EDGE,"E71.4"),sQuery(id+"F5.wireOp",EDGE,"E71.5"),sQuery(id+"F5.wireOp",EDGE,"E71.6"),sQuery(id+"F5.wireOp",EDGE,"E71.7")])],"isStart":false})});
            var Q3;
            Q3=makeQuery(id+"F6.boolean.opBoolean","SPLIT",FACE,{"disambiguationData":[TD([makeQuery(id+"F2.opExtrude","SWEPT_FACE",FACE,{"disambiguationData":[OSD([sQuery(id+"F1.wireOp",EDGE,"E32.MirrorCS")])]})])],"derivedFrom":makeQuery(id+"F6.opExtrude","CAP_FACE",FACE,{"disambiguationData":[OSD([sQuery(id+"F5.wireOp",EDGE,"E71.0"),sQuery(id+"F5.wireOp",EDGE,"E71.1"),sQuery(id+"F5.wireOp",EDGE,"E71.2"),sQuery(id+"F5.wireOp",EDGE,"E71.3"),sQuery(id+"F5.wireOp",EDGE,"E71.4"),sQuery(id+"F5.wireOp",EDGE,"E71.5"),sQuery(id+"F5.wireOp",EDGE,"E71.6"),sQuery(id+"F5.wireOp",EDGE,"E71.7")])],"isStart":false})});
            var Q4;
            Q4=makeQuery(id+"F6.boolean.opBoolean","SPLIT",FACE,{"disambiguationData":[TD([makeQuery(id+"F2.opExtrude","SWEPT_FACE",FACE,{"disambiguationData":[OSD([sQuery(id+"F1.wireOp",EDGE,"E10.bottom")])]})])],"derivedFrom":makeQuery(id+"F6.opExtrude","CAP_FACE",FACE,{"disambiguationData":[OSD([sQuery(id+"F5.wireOp",EDGE,"E71.0"),sQuery(id+"F5.wireOp",EDGE,"E71.1"),sQuery(id+"F5.wireOp",EDGE,"E71.2"),sQuery(id+"F5.wireOp",EDGE,"E71.3"),sQuery(id+"F5.wireOp",EDGE,"E71.4"),sQuery(id+"F5.wireOp",EDGE,"E71.5"),sQuery(id+"F5.wireOp",EDGE,"E71.6"),sQuery(id+"F5.wireOp",EDGE,"E71.7")])],"isStart":false})});
            var Q5;
            Q5=makeQuery(id+"F6.boolean.opBoolean","SPLIT",FACE,{"disambiguationData":[TD([makeQuery(id+"F2.opExtrude","SWEPT_FACE",FACE,{"disambiguationData":[OSD([sQuery(id+"F1.wireOp",EDGE,"E2.bottom")])]})])],"derivedFrom":makeQuery(id+"F6.opExtrude","CAP_FACE",FACE,{"disambiguationData":[OSD([sQuery(id+"F5.wireOp",EDGE,"E71.0"),sQuery(id+"F5.wireOp",EDGE,"E71.1"),sQuery(id+"F5.wireOp",EDGE,"E71.2"),sQuery(id+"F5.wireOp",EDGE,"E71.3"),sQuery(id+"F5.wireOp",EDGE,"E71.4"),sQuery(id+"F5.wireOp",EDGE,"E71.5"),sQuery(id+"F5.wireOp",EDGE,"E71.6"),sQuery(id+"F5.wireOp",EDGE,"E71.7")])],"isStart":false})});
            var Q6;
            Q6=makeQuery(id+"F6.boolean.opBoolean","SPLIT",FACE,{"disambiguationData":[TD([makeQuery(id+"F2.opExtrude","SWEPT_FACE",FACE,{"disambiguationData":[OSD([sQuery(id+"F1.wireOp",EDGE,"E22.MirrorCS")])]})])],"derivedFrom":makeQuery(id+"F6.opExtrude","CAP_FACE",FACE,{"disambiguationData":[OSD([sQuery(id+"F5.wireOp",EDGE,"E71.0"),sQuery(id+"F5.wireOp",EDGE,"E71.1"),sQuery(id+"F5.wireOp",EDGE,"E71.2"),sQuery(id+"F5.wireOp",EDGE,"E71.3"),sQuery(id+"F5.wireOp",EDGE,"E71.4"),sQuery(id+"F5.wireOp",EDGE,"E71.5"),sQuery(id+"F5.wireOp",EDGE,"E71.6"),sQuery(id+"F5.wireOp",EDGE,"E71.7")])],"isStart":false})});
            fillet(context, id + "F20", {"entities" : qUnion([Q0, Q1, Q2, Q3, Q4, Q5, Q6]), "radius" : 12.7 * mm, "tangentPropagation" : true, "allowEdgeOverflow" : false});
        }
    });
